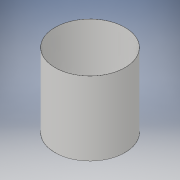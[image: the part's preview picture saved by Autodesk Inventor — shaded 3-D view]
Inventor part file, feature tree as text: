
AUTODESK INVENTOR PART (.ipt)
format: ipt  version: 2018 (Build 220112000, 112)  size: 93,696 bytes
history: native  units: in
note: dims shown in document units (in); Inventor stores cm internally (conversion verified against a paired STEP export)
features: extrude x1, sketch x1
ambient origin geometry x8: Origin, YZ Plane, XZ Plane, XY Plane, X Axis, Y Axis, Z Axis, Center Point
bodies: Solid1 (feature_tree)
feature tree (2):
  extrude  "Extrusion1"  Depth=19.0in
  sketch  "Sketch1"  dims[d0=18.0in d1=18.065in d2=19.0in d3=0.0in]
